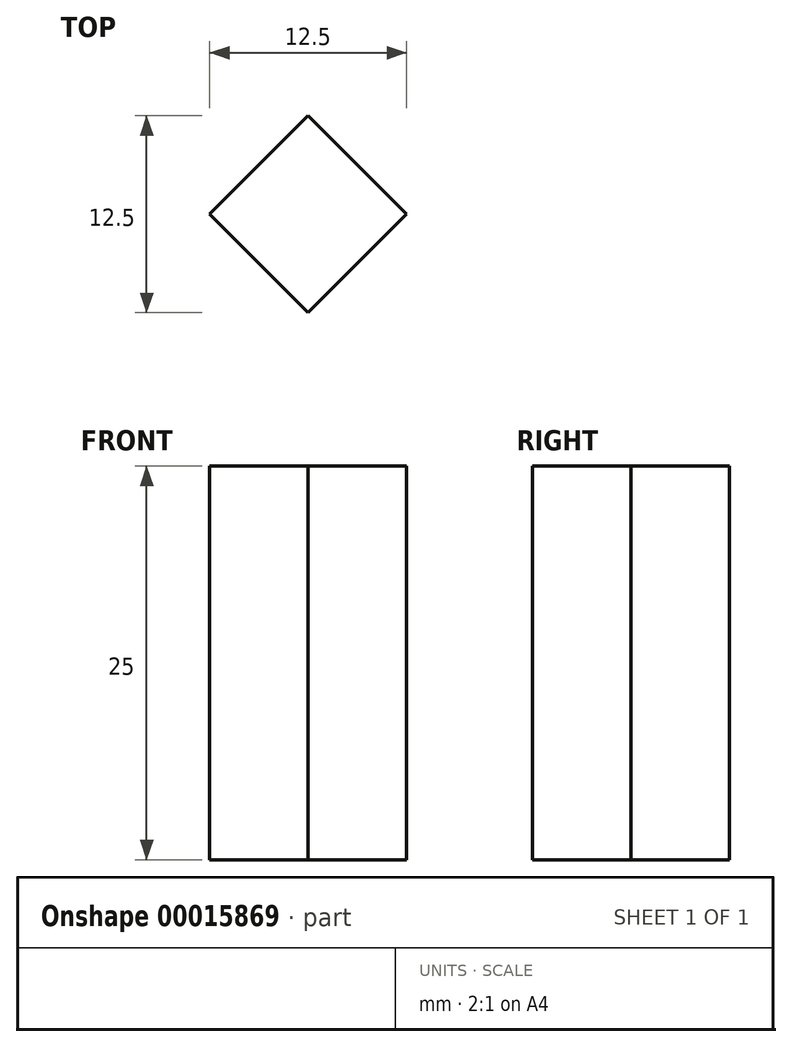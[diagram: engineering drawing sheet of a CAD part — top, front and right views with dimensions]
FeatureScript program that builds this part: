
annotation { "Feature Type Name" : "Feature", "Feature Type Description" : "" }
export const myFeature = defineFeature(function(context is Context, id is Id, definition is map)
    precondition{}
    {
        {
            var Q0;
            Q0=qCreatedBy(makeId("Top.planeOp"),FACE);
            var sketch = newSketch(context, id + "F0", { "sketchPlane" : qUnion([Q0])});
            skCircle(sketch, "E0.cCircle", {"center": v(0, 0) * mm, "radius": 6.25 * mm, "construction": true});
            skLineSegment(sketch, "E0.0", {"start": v(6.25, 0) * mm, "end": v(0, -6.25) * mm});
            skLineSegment(sketch, "E0.1", {"start": v(0, -6.25) * mm, "end": v(-6.25, 0) * mm});
            skLineSegment(sketch, "E0.2", {"start": v(-6.25, 0) * mm, "end": v(0, 6.25) * mm});
            skLineSegment(sketch, "E0.3", {"start": v(0, 6.25) * mm, "end": v(6.25, 0) * mm});
            skSolve(sketch);
        }
        {
            var Q0;
            Q0 = qSketchRegion(id + "F0", true);
            extrude(context, id + "F1", {"entities" : qUnion([Q0]), "depth" : 25 * mm});
        }
    });
